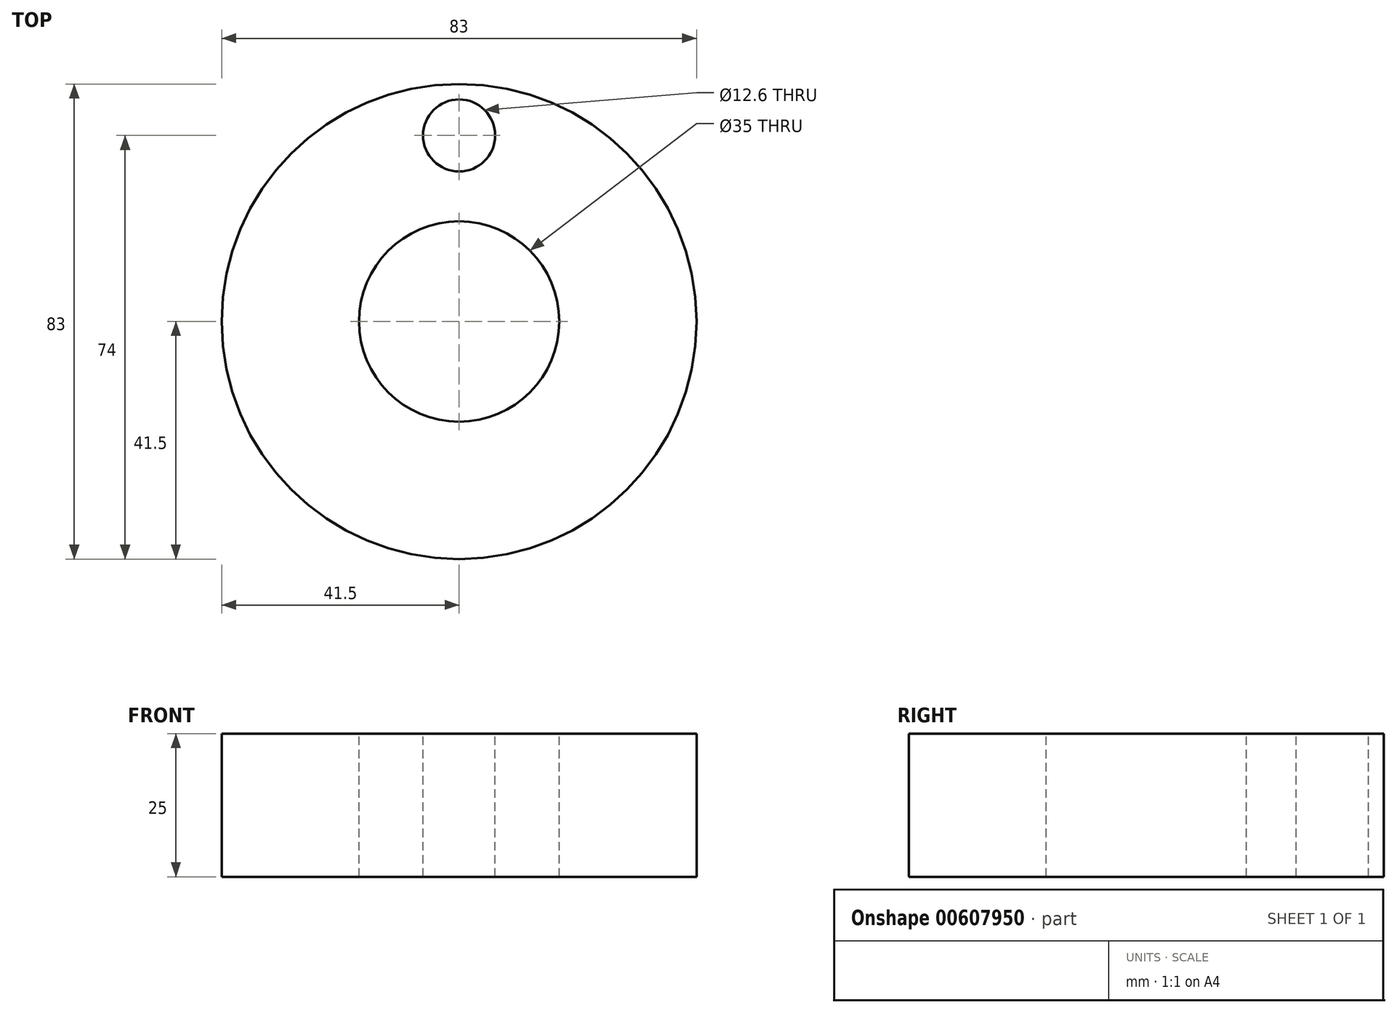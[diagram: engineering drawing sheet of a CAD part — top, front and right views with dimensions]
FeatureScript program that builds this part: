
annotation { "Feature Type Name" : "Feature", "Feature Type Description" : "" }
export const myFeature = defineFeature(function(context is Context, id is Id, definition is map)
    precondition{}
    {
        {
            var Q0;
            Q0=qCreatedBy(makeId("Top.planeOp"),FACE);
            var sketch = newSketch(context, id + "F0", { "sketchPlane" : qUnion([Q0])});
            skCircle(sketch, "E0", {"center": v(0, 0) * mm, "radius": 41.5 * mm});
            skSolve(sketch);
        }
        {
            var Q0;
            Q0 = qSketchRegion(id + "F0", true);
            extrude(context, id + "F1", {"entities" : qUnion([Q0]), "depth" : 25 * mm, "offsetDistance" : 25 * mm});
        }
        {
            var Q0;
            Q0=makeQuery(id+"F1.opExtrude","CAP_FACE",FACE,{"disambiguationData":[OSD([sQuery(id+"F0.wireOp",EDGE,"E0")])],"isStart":false});
            var sketch = newSketch(context, id + "F2", { "sketchPlane" : qUnion([Q0])});
            skCircle(sketch, "E1", {"center": v(0, 0) * mm, "radius": 32.5 * mm, "construction": true});
            skLineSegment(sketch, "E2", {"start": v(0, 32.5) * mm, "end": v(0, 0) * mm, "construction": true});
            skSolve(sketch);
        }
        {
            var Q0;
            Q0=sQuery(id+"F2.wireOp",VERTEX,"E2.start");
            var Q1;
            Q1=makeQuery(id+"F1.opExtrude","SWEPT_BODY",BODY,{"disambiguationData":[OSD([sQuery(id+"F0.wireOp",EDGE,"E0")])]});
            hole(context, id + "F3", {"style" : HoleStyle.SIMPLE, "endStyle" : HoleEndStyle.THROUGH, "standardTappedOrClearance" : lookupTablePath({ "standard" : "ISO", "fit" : "Close", "size" : "M12", "type" : "Clearance" }), "standardBlindInLast" : lookupTablePath({ "fit" : "Close", "standard" : "ISO", "size" : "M12", "type" : "Clearance" }), "holeDiameter" : 12.6 * mm, "majorDiameter" : 5 * mm, "isTappedThrough" : true, "tappedDepth" : 12 * mm, "tapClearance" : 3, "locations" : qUnion([Q0]), "scope" : qUnion([Q1])});
        }
        {
            var Q0;
            Q0=makeQuery(id+"F1.opExtrude","CAP_FACE",FACE,{"disambiguationData":[OSD([sQuery(id+"F0.wireOp",EDGE,"E0")])],"isStart":false});
            var sketch = newSketch(context, id + "F4", { "sketchPlane" : qUnion([Q0])});
            skCircle(sketch, "E3", {"center": v(0, 0) * mm, "radius": 17.5 * mm});
            skSolve(sketch);
        }
        {
            var Q0;
            Q0=makeQuery(id+"F4.imprint","IMPRINT",FACE,{"disambiguationData":[TD([[makeQuery(id+"F4.imprint","IMPRINT",EDGE,{"derivedFrom":sQuery(id+"F4.wireOp",EDGE,"E3")}),1.0]])]});
            extrude(context, id + "F5", {"entities" : qUnion([Q0]), "operationType" : NewBodyOperationType.REMOVE, "endBound" : BoundingType.THROUGH_ALL, "oppositeDirection" : true, "depth" : 25 * mm, "offsetDistance" : 25 * mm});
        }
    });
